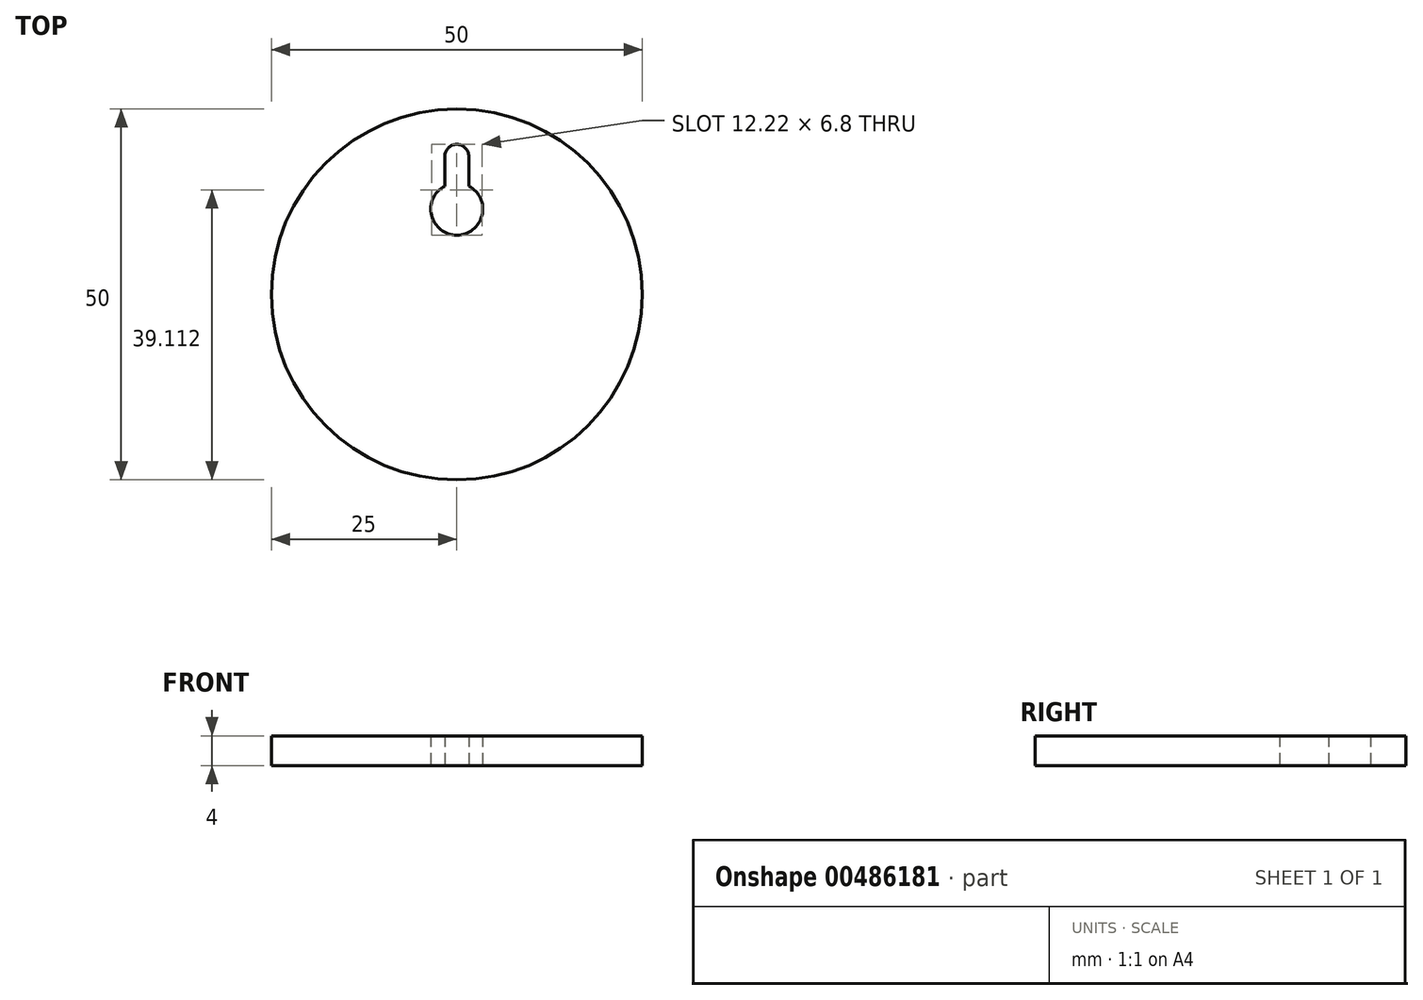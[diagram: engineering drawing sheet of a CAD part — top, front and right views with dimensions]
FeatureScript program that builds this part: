
annotation { "Feature Type Name" : "Feature", "Feature Type Description" : "" }
export const myFeature = defineFeature(function(context is Context, id is Id, definition is map)
    precondition{}
    {
        {
            var Q0;
            Q0=qCreatedBy(makeId("Top.planeOp"),FACE);
            var sketch = newSketch(context, id + "F0", { "sketchPlane" : qUnion([Q0])});
            skCircle(sketch, "E0", {"center": v(0, 0) * mm, "radius": 25 * mm});
            skArc(sketch, "E1", {"start": v(-1.63, 14.6) * mm, "mid": v(0, 8) * mm, "end": v(1.62, 14.6) * mm});
            skLineSegment(sketch, "E2.left", {"start": v(1.62, 14.6) * mm, "end": v(1.62, 18.6) * mm});
            skLineSegment(sketch, "E2.right", {"start": v(-1.63, 14.6) * mm, "end": v(-1.63, 18.6) * mm});
            skPoint(sketch, "E2.middle", {"position": v(0, 16.6) * mm});
            skArc(sketch, "E3", {"start": v(1.62, 18.6) * mm, "mid": v(0, 20.22) * mm, "end": v(-1.63, 18.6) * mm});
            skSolve(sketch);
        }
        {
            var Q0;
            Q0=makeQuery(id+"F0.imprint","IMPRINT",FACE,{"disambiguationData":[TD([[makeQuery(id+"F0.imprint","IMPRINT",EDGE,{"derivedFrom":sQuery(id+"F0.wireOp",EDGE,"E0")}),1.0]])]});
            extrude(context, id + "F1", {"entities" : qUnion([Q0]), "depth" : 4 * mm});
        }
    });
